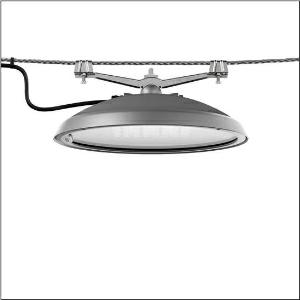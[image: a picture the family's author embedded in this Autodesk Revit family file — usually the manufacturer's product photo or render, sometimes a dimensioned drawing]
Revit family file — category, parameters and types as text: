
# Revit family: dl_50_iq_mini___st1_0s_5xa248w21f08ge_17b4
name_source: partatom
category: Lighting Fixtures
units: mm (PartAtom-declared; Revit-internal decimal feet)

## family parameters
Cut with Voids When Loaded = No
Host = Face
Light Source = No
Part Type = Normal
Room Calculation Point = No
Round Connector Dimension = Use Diameter
Shared = No

## types (1)
- --- (1 x LED, 4580 lm, 35.2 W, 2200K)
    Apparent Load = 35 VA
    CIE Flux Codes = 37 72 97 100 100
    Color Rendering = 70
    Color Temperature = 2200K
    Default Elevation = 1800 mm
    Description = DL 50 iQ mini, catenary luminaire, primary light control with lens, of PMMA, primary optical cover: cover, of toughened safety glass, transparent, light distribution: ST1.0s, light emission: direct distribution, primary light characteristic: symmetric, installation type: suspended mounting, LED, High Power LED, rated luminous flux: 4.580lm, luminous efficacy: 130lm/W, light colour: 722, colour temperature: 2200K, control gear: iQ Street-Remote, control: optimised constant luminous flux control (CLO 2.0), Desk-Remote (wireless, voltage-free reading and setting of iQ features in the workshop via application-optimized NFC function/RFID function), Light-Fading, Smart-Wire, Night-Set, Lumen-Switch, Temp-Guard, Auto-Match, Street-Remote, mains connection: 230..240V, AC, 50/60Hz, start of lifetime: 35W, end of service life: 36W, reduction: 17W, luminaire housing, of diecast aluminium, powder-coated, SITECO metallic grey (DB 702S), diameter: 500mm, height: 115mm, mounting height: 4..12m, protection rating (complete): IP66, insulation class (complete): insulation class II (safety insulation), certification: CE, ENEC, ENEC+, VDE, impact resistance: IK08, permissible operating ambient temperature for outdoor applications: -25..+40°C, standard-compliant lighting for roads and squares, packaging unit: 1 piece

Light Distribution: ST1.0s
    Height = 124 mm  [stored 0.406824 ft]
    Lamp = 1 x LED
    Lamp Light Flux = 4580 lm
    Lamp Power = 35.2 W
    Lamp count = 1
    Length = 500 mm
    Luminous efficacy = 130 lm/W
    Manufacturer = Siteco
    ModVariant = No
    Model = 5XA248W21F08GE
    Number of Poles = 1
    OnlyDefault = Yes
    Power Factor = 1
    Product Name = DL 50 iQ mini | ST1.0s
    Product group = catenary luminaire
    ProductGroupID = 6300
    Protection Class = Protection class II
    Protection Degree = IP 66
    RLX_Detail_Level = 1
    RLX_Emergency_Light_Flux = 0 lm
    RLX_Emergency_Type = 0
    RLX_Emergency_Type_DB = No
    RlxData = <blob elided: 123545 chars, md5=e5affdfb>
    Socket = socket
    Standby Power = 0 W
    System Light Flux = 4580 lm
    System Power = 35 W
    Type Comments = factory setting: luminous flux: 100 % | dim-lin: 254 | 365 mA
    Type Image = l_1242791.jpg
    URL = http://relux.com
    VarID = @adj_141957
    Voltage = 0 V
    Weight = 0.00 kg
    Width = 0 mm  [stored 0 ft]

note: [stored X ft] marks values corroborated as IEEE doubles in the binary element streams (Revit-internal decimal feet)

## geometry (parser evidence)
native form markers: Blend x4, Sweep x13
no freeform markers — native parametric forms only
